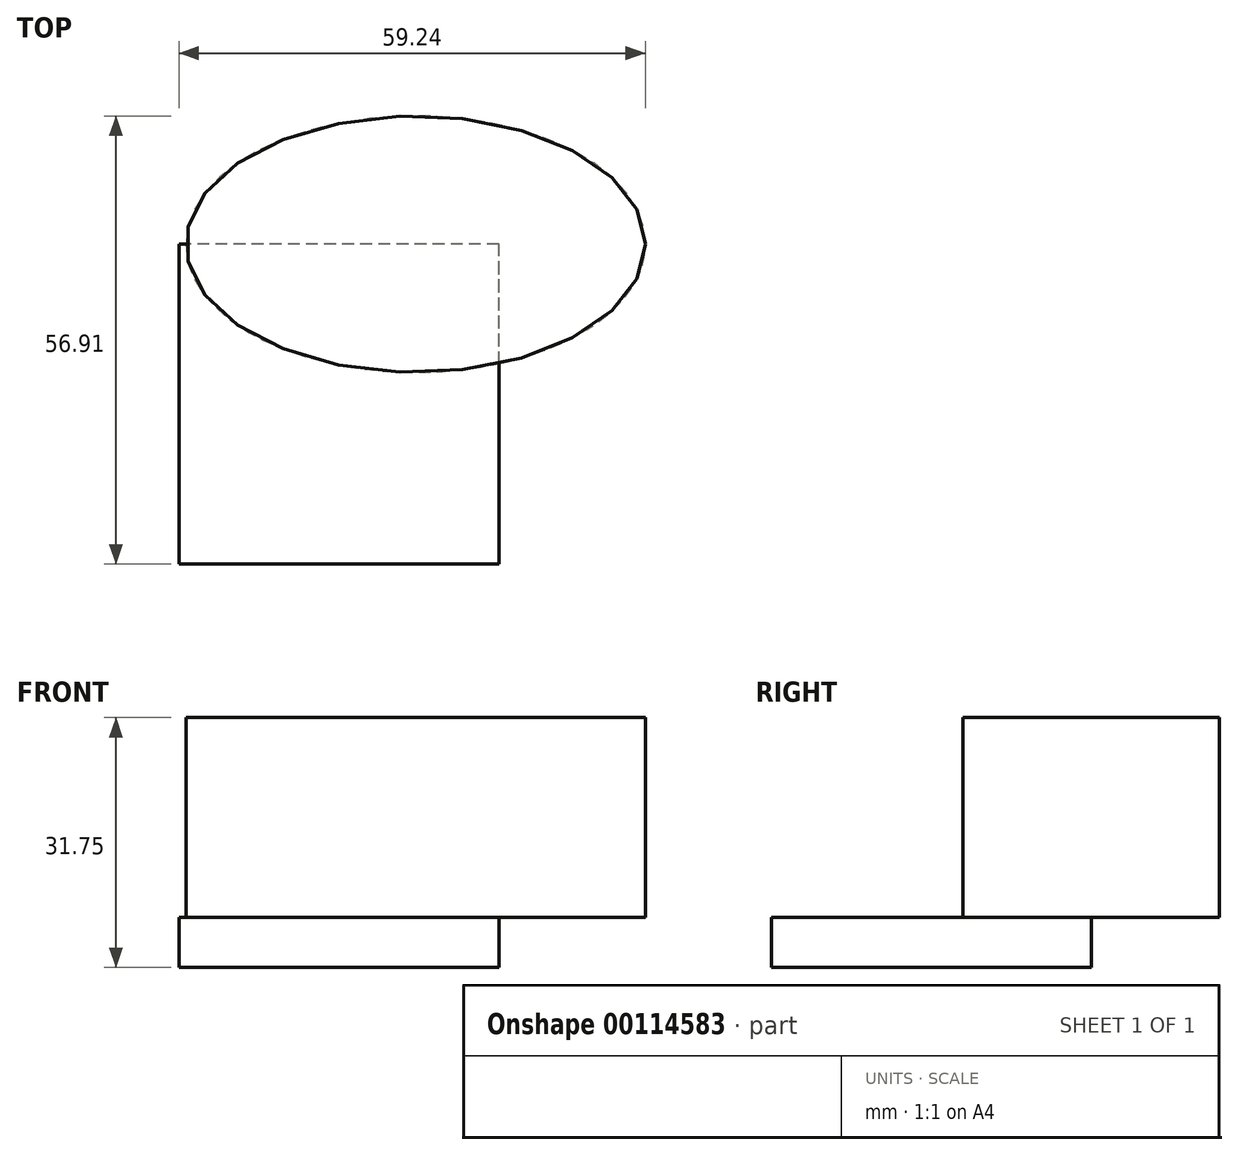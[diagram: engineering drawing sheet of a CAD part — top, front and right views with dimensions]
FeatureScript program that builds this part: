
annotation { "Feature Type Name" : "Feature", "Feature Type Description" : "" }
export const myFeature = defineFeature(function(context is Context, id is Id, definition is map)
    precondition{}
    {
        {
            var Q0;
            Q0=qCreatedBy(makeId("Top.planeOp"),FACE);
            var sketch = newSketch(context, id + "F0", { "sketchPlane" : qUnion([Q0])});
            skLineSegment(sketch, "E0.bottom", {"start": v(20.32, -20.32) * mm, "end": v(-20.32, -20.32) * mm});
            skLineSegment(sketch, "E0.top", {"start": v(20.32, 20.32) * mm, "end": v(-20.32, 20.32) * mm});
            skLineSegment(sketch, "E0.left", {"start": v(20.32, -20.32) * mm, "end": v(20.32, 20.32) * mm});
            skLineSegment(sketch, "E0.right", {"start": v(-20.32, -20.32) * mm, "end": v(-20.32, 20.32) * mm});
            skPoint(sketch, "E0.middle", {"position": v(0, 0) * mm});
            skSolve(sketch);
        }
        {
            var Q0;
            Q0 = qSketchRegion(id + "F0", true);
            var Q1;
            Q1 = qSketchRegion(id + "F2", true);
            extrude(context, id + "F1", {"entities" : qUnion([Q0, Q1]), "depth" : 6.35 * mm});
        }
        {
            var Q0;
            Q0=qCreatedBy(makeId("Top.planeOp"),FACE);
            var sketch = newSketch(context, id + "F2", { "sketchPlane" : qUnion([Q0])});
            skLineSegment(sketch, "E1.bottom", {"start": v(17.78, -17.78) * mm, "end": v(-17.78, -17.78) * mm});
            skLineSegment(sketch, "E1.top", {"start": v(17.78, 17.78) * mm, "end": v(-17.78, 17.78) * mm});
            skLineSegment(sketch, "E1.left", {"start": v(17.78, -17.78) * mm, "end": v(17.78, 17.78) * mm});
            skLineSegment(sketch, "E1.right", {"start": v(-17.78, -17.78) * mm, "end": v(-17.78, 17.78) * mm});
            skPoint(sketch, "E1.middle", {"position": v(0, 0) * mm});
            skSolve(sketch);
        }
        {
            var Q0;
            Q0 = qSketchRegion(id + "F2", true);
            extrude(context, id + "F3", {"entities" : qUnion([Q0]), "operationType" : NewBodyOperationType.ADD, "depth" : 1.27 * mm});
        }
        {
            var Q0;
            Q0=makeQuery(id+"F1.opExtrude","CAP_FACE",FACE,{"disambiguationData":[OSD([sQuery(id+"F0.wireOp",EDGE,"E0.bottom"),sQuery(id+"F0.wireOp",EDGE,"E0.top"),sQuery(id+"F0.wireOp",EDGE,"E0.left"),sQuery(id+"F0.wireOp",EDGE,"E0.right")])],"isStart":false});
            var sketch = newSketch(context, id + "F4", { "sketchPlane" : qUnion([Q0])});
            skEllipse(sketch, "E2", {"center": v(9.75, 20.32) * mm, "majorRadius": 16.27 * mm, "minorRadius": 29.17 * mm, "majorAxis": v(0, -1)});
            skSolve(sketch);
        }
        {
            var Q0;
            Q0 = qSketchRegion(id + "F4", true);
            extrude(context, id + "F5", {"entities" : qUnion([Q0]), "operationType" : NewBodyOperationType.ADD, "depth" : 25.4 * mm, "offsetDistance" : 25.4 * mm});
        }
    });
